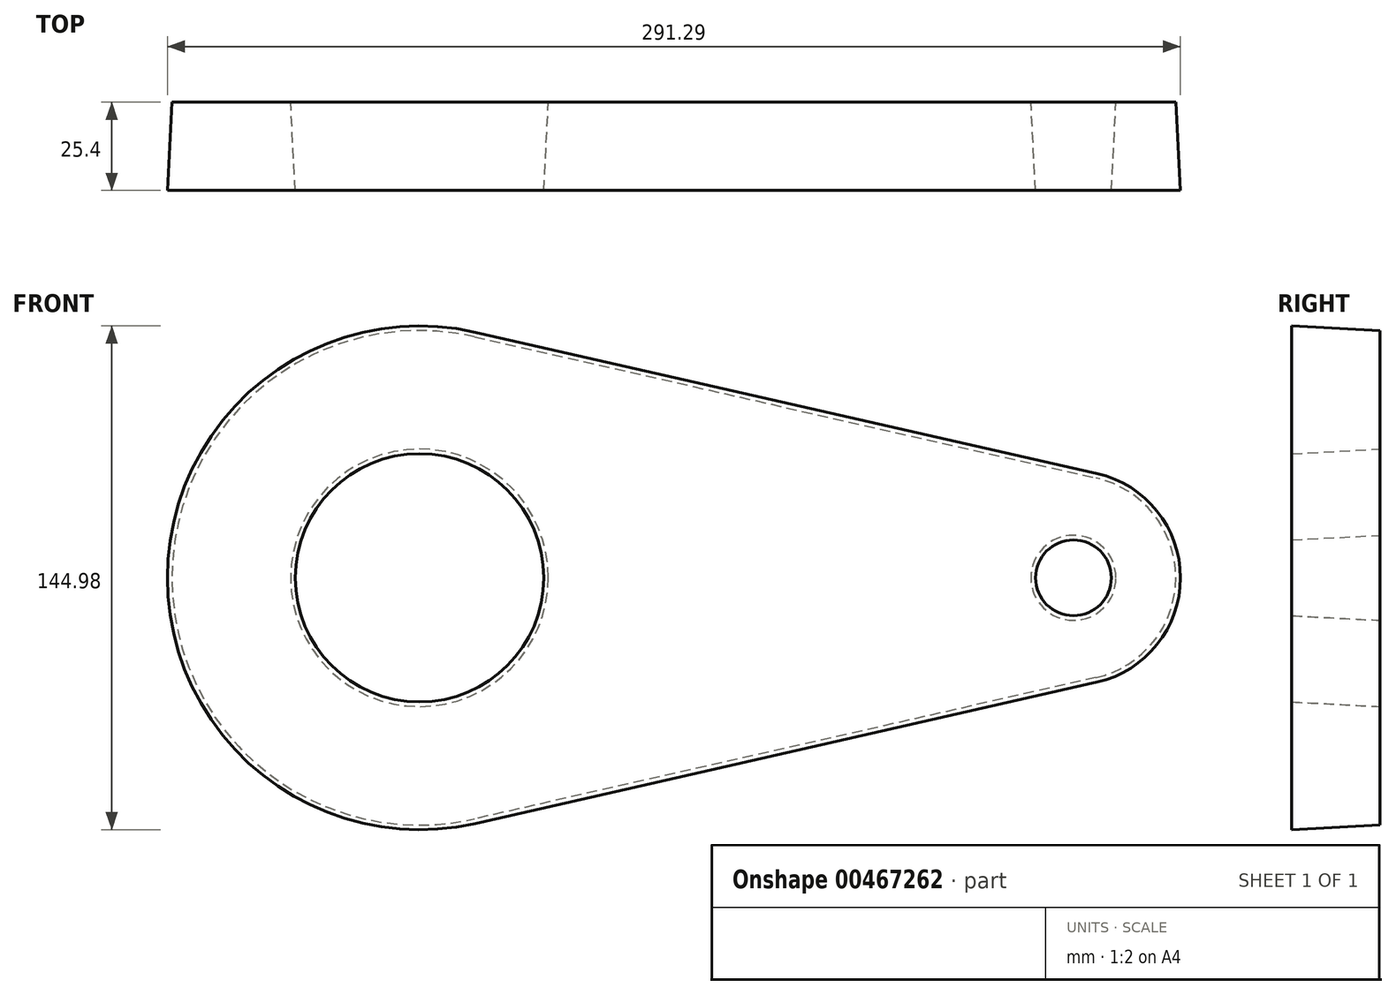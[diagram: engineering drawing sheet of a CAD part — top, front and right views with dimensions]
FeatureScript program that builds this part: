
annotation { "Feature Type Name" : "Feature", "Feature Type Description" : "" }
export const myFeature = defineFeature(function(context is Context, id is Id, definition is map)
    precondition{}
    {
        {
            var Q0;
            Q0=qCreatedBy(makeId("Front.planeOp"),FACE);
            var sketch = newSketch(context, id + "F0", { "sketchPlane" : qUnion([Q0])});
            skCircle(sketch, "E0", {"center": v(0, 0) * mm, "radius": 71.15 * mm});
            skCircle(sketch, "E1", {"center": v(188.04, 0) * mm, "radius": 29.43 * mm});
            skLineSegment(sketch, "E2", {"start": v(15.79, 69.38) * mm, "end": v(194.57, 28.7) * mm});
            skLineSegment(sketch, "E3.MirrorCS", {"start": v(15.79, -69.38) * mm, "end": v(194.57, -28.7) * mm});
            skCircle(sketch, "E4", {"center": v(0, 0) * mm, "radius": 37.05 * mm});
            skCircle(sketch, "E5", {"center": v(188.04, 0) * mm, "radius": 12.23 * mm});
            skSolve(sketch);
        }
        {
            var Q0;
            Q0 = qSketchRegion(id + "F0", true);
            extrude(context, id + "F1", {"entities" : qUnion([Q0]), "depth" : 25.4 * mm, "hasDraft" : true, "draftAngle" : 3 * degree});
        }
    });
